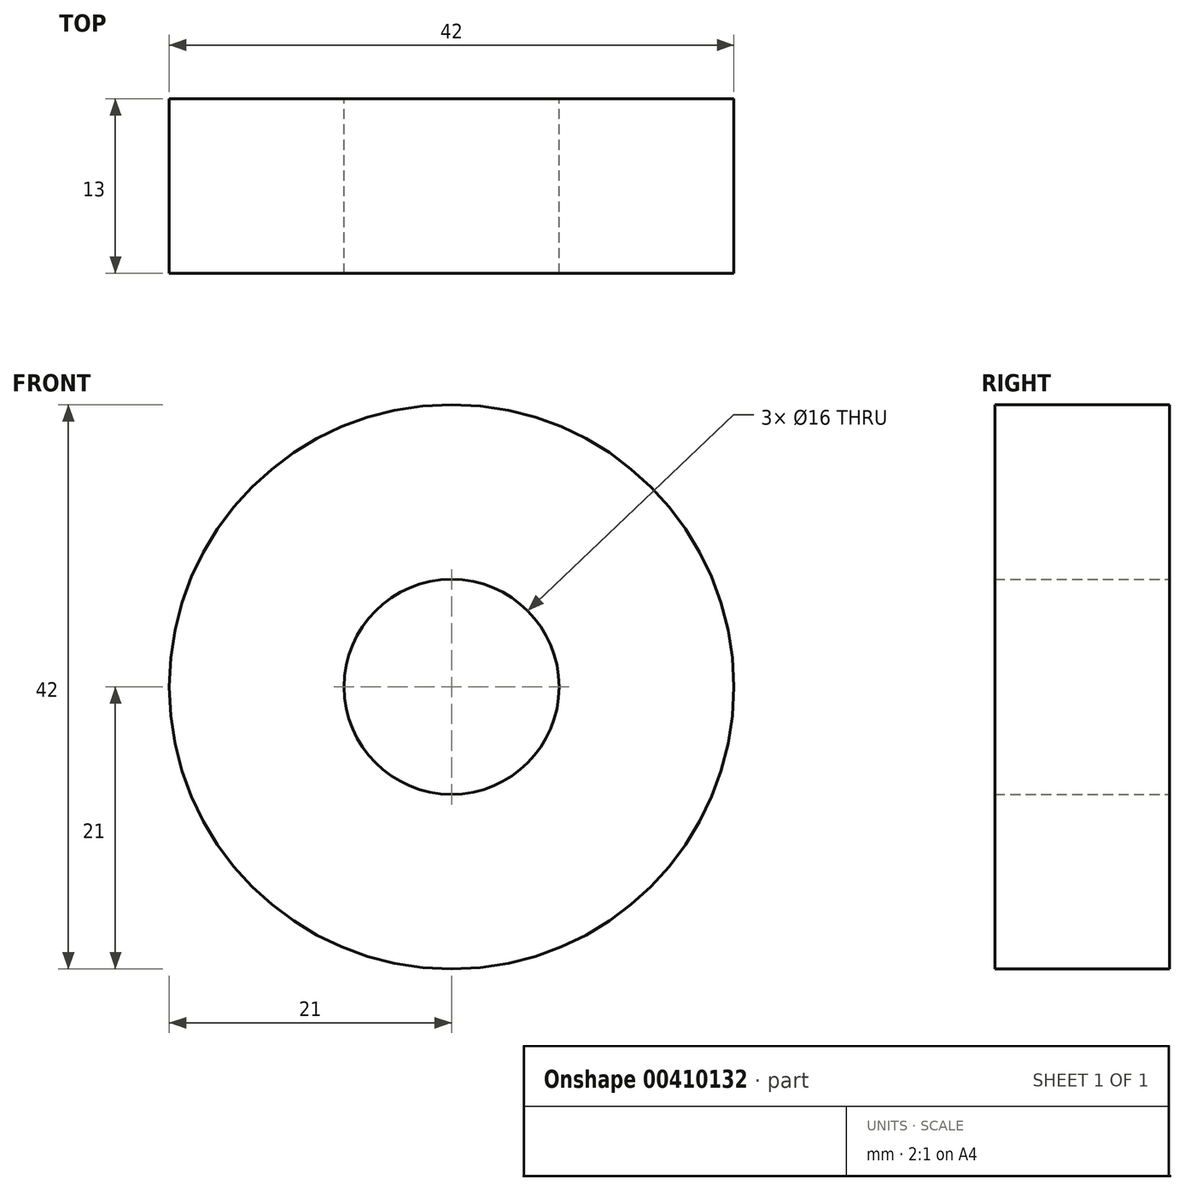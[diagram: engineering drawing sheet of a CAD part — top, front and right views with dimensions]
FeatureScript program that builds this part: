
annotation { "Feature Type Name" : "Feature", "Feature Type Description" : "" }
export const myFeature = defineFeature(function(context is Context, id is Id, definition is map)
    precondition{}
    {
        {
            var Q0;
            Q0=qCreatedBy(makeId("Front.planeOp"),FACE);
            var sketch = newSketch(context, id + "F0", { "sketchPlane" : qUnion([Q0])});
            skCircle(sketch, "E0", {"center": v(0, 0) * mm, "radius": 8 * mm});
            skCircle(sketch, "E1", {"center": v(0, 0) * mm, "radius": 21 * mm});
            skSolve(sketch);
        }
        {
            var Q0;
            Q0=qSketchRegion(id+"F0",true);
            extrude(context, id + "F1", {"entities" : qUnion([Q0]), "depth" : 13 * mm});
        }
    });
